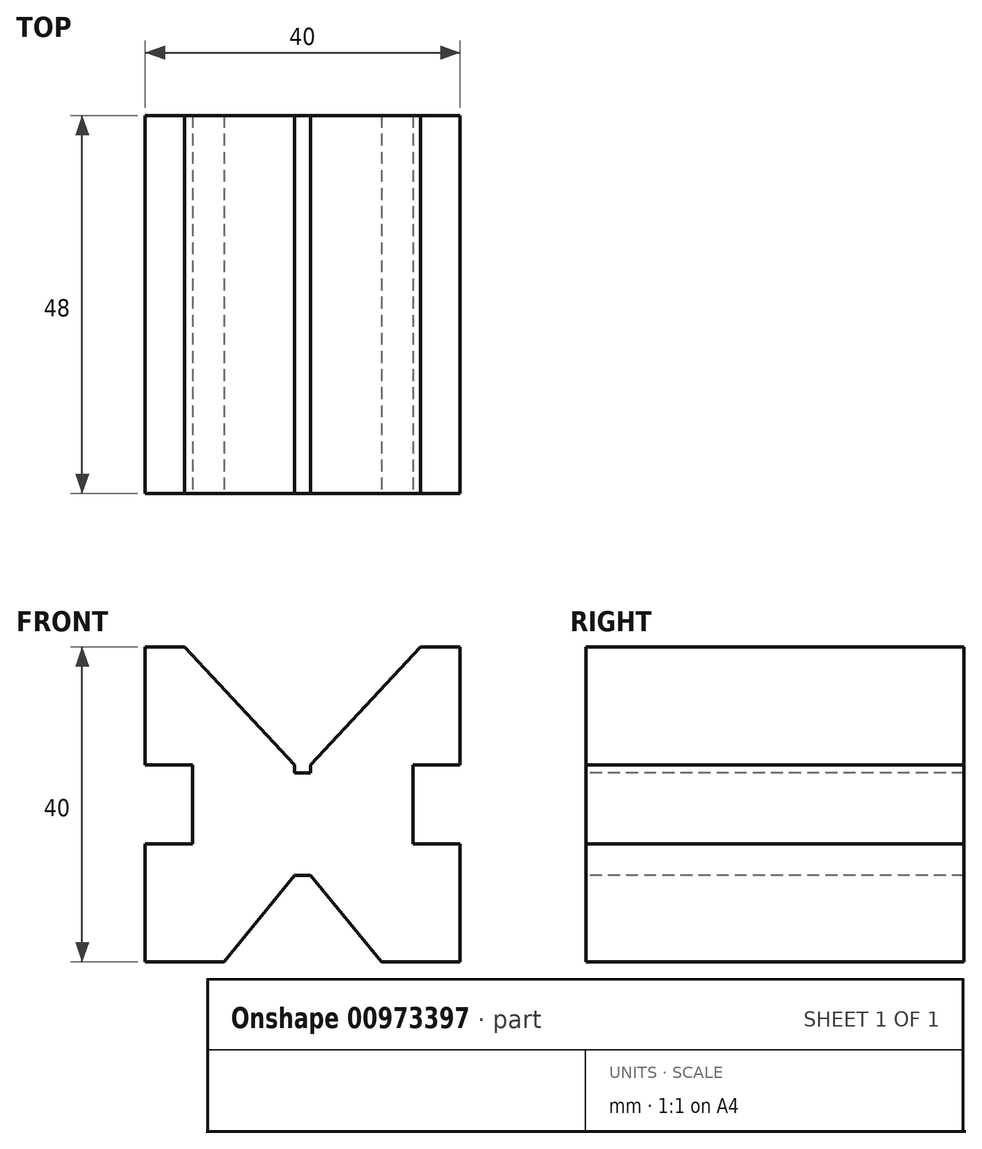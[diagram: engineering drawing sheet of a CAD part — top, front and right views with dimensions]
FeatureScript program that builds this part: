
annotation { "Feature Type Name" : "Feature", "Feature Type Description" : "" }
export const myFeature = defineFeature(function(context is Context, id is Id, definition is map)
    precondition{}
    {
        {
            var Q0;
            Q0=qCreatedBy(makeId("Front.planeOp"),FACE);
            var sketch = newSketch(context, id + "F0", { "sketchPlane" : qUnion([Q0])});
            skLineSegment(sketch, "E0", {"start": v(0, 4.45) * mm, "end": v(-1, 4.45) * mm});
            skLineSegment(sketch, "E1", {"start": v(-1, 4.45) * mm, "end": v(-1, 5.45) * mm});
            skLineSegment(sketch, "E2", {"start": v(-15, 20.45) * mm, "end": v(-1, 5.45) * mm});
            skLineSegment(sketch, "E3", {"start": v(-15, 20.45) * mm, "end": v(-20, 20.45) * mm});
            skLineSegment(sketch, "E4", {"start": v(-20, 20.45) * mm, "end": v(-20, 5.45) * mm});
            skLineSegment(sketch, "E5", {"start": v(-20, 5.45) * mm, "end": v(-14, 5.45) * mm});
            skLineSegment(sketch, "E6", {"start": v(-14, 5.45) * mm, "end": v(-14, -4.55) * mm});
            skLineSegment(sketch, "E7", {"start": v(-14, -4.55) * mm, "end": v(-20, -4.55) * mm});
            skLineSegment(sketch, "E8", {"start": v(-20, -4.55) * mm, "end": v(-20, -19.55) * mm});
            skLineSegment(sketch, "E9", {"start": v(-20, -19.55) * mm, "end": v(-10, -19.55) * mm});
            skLineSegment(sketch, "E10", {"start": v(-1, -8.55) * mm, "end": v(0, -8.55) * mm});
            skLineSegment(sketch, "E11", {"start": v(-1, -8.55) * mm, "end": v(-10, -19.55) * mm});
            skLineSegment(sketch, "E12.MirrorCS", {"start": v(1, -8.55) * mm, "end": v(10, -19.55) * mm});
            skLineSegment(sketch, "E13.MirrorCS", {"start": v(1, -8.55) * mm, "end": v(0, -8.55) * mm});
            skLineSegment(sketch, "E14.MirrorCS", {"start": v(20, -19.55) * mm, "end": v(10, -19.55) * mm});
            skLineSegment(sketch, "E15.MirrorCS", {"start": v(20, -4.55) * mm, "end": v(20, -19.55) * mm});
            skLineSegment(sketch, "E16.MirrorCS", {"start": v(14, -4.55) * mm, "end": v(20, -4.55) * mm});
            skLineSegment(sketch, "E17.MirrorCS", {"start": v(14, 5.45) * mm, "end": v(14, -4.55) * mm});
            skLineSegment(sketch, "E18.MirrorCS", {"start": v(20, 5.45) * mm, "end": v(14, 5.45) * mm});
            skLineSegment(sketch, "E19.MirrorCS", {"start": v(20, 20.45) * mm, "end": v(20, 5.45) * mm});
            skLineSegment(sketch, "E20.MirrorCS", {"start": v(15, 20.45) * mm, "end": v(20, 20.45) * mm});
            skLineSegment(sketch, "E21.MirrorCS", {"start": v(15, 20.45) * mm, "end": v(1, 5.45) * mm});
            skLineSegment(sketch, "E22.MirrorCS", {"start": v(1, 4.45) * mm, "end": v(1, 5.45) * mm});
            skLineSegment(sketch, "E23.MirrorCS", {"start": v(0, 4.45) * mm, "end": v(1, 4.45) * mm});
            skSolve(sketch);
        }
        {
            var Q0;
            Q0=makeQuery(id+"F0.imprint","IMPRINT",FACE,{"disambiguationData":[TD([[makeQuery(id+"F0.imprint","IMPRINT",EDGE,{"derivedFrom":sQuery(id+"F0.wireOp",EDGE,"E0")}),1.0]])]});
            extrude(context, id + "F1", {"entities" : qUnion([Q0]), "oppositeDirection" : true, "depth" : 48 * mm, "offsetDistance" : 25 * mm});
        }
    });
